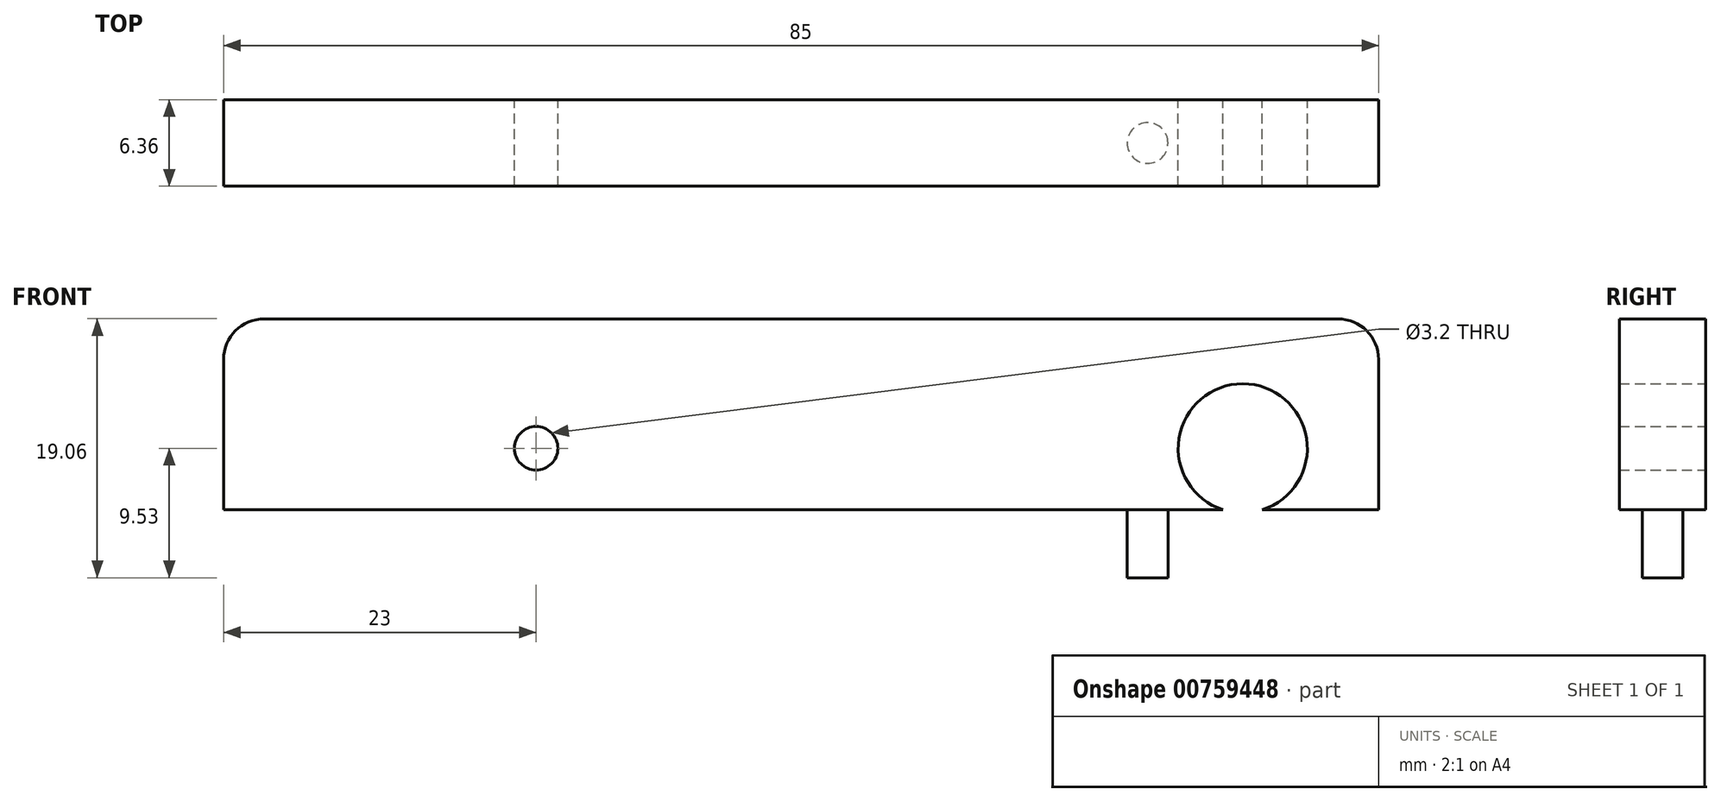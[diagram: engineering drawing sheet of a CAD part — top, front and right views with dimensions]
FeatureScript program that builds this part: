
annotation { "Feature Type Name" : "Feature", "Feature Type Description" : "" }
export const myFeature = defineFeature(function(context is Context, id is Id, definition is map)
    precondition{}
    {
        {
            var Q0;
            Q0=qCreatedBy(makeId("Front.planeOp"),FACE);
            var sketch = newSketch(context, id + "F0", { "sketchPlane" : qUnion([Q0])});
            skLineSegment(sketch, "E0.bottom", {"start": v(42.5, 9.53) * mm, "end": v(-42.5, 9.53) * mm});
            skLineSegment(sketch, "E0.top", {"start": v(42.5, -9.53) * mm, "end": v(-42.5, -9.53) * mm});
            skLineSegment(sketch, "E0.left", {"start": v(42.5, 9.53) * mm, "end": v(42.5, -9.52) * mm});
            skLineSegment(sketch, "E0.right", {"start": v(-42.5, 9.53) * mm, "end": v(-42.5, -9.53) * mm});
            skPoint(sketch, "E0.middle", {"position": v(0, 0) * mm});
            skPoint(sketch, "E1.center.orphan", {"position": v(32.5, 0) * mm});
            skCircle(sketch, "E2", {"center": v(32.5, 0) * mm, "radius": 4.75 * mm});
            skCircle(sketch, "E3", {"center": v(-19.5, 0) * mm, "radius": 1.6 * mm});
            skSolve(sketch);
        }
        {
            var Q0;
            Q0=makeQuery(id+"F0.imprint","IMPRINT",FACE,{"disambiguationData":[TD([[makeQuery(id+"F0.imprint","IMPRINT",EDGE,{"derivedFrom":sQuery(id+"F0.wireOp",EDGE,"E0.bottom")}),1.0]])]});
            extrude(context, id + "F1", {"entities" : qUnion([Q0]), "endBound" : BoundingType.SYMMETRIC, "depth" : 6.35 * mm, "offsetDistance" : 25 * mm});
        }
        {
            var Q0;
            Q0=makeQuery(id+"F1.opExtrude","SWEPT_FACE",FACE,{"disambiguationData":[OSD([sQuery(id+"F0.wireOp",EDGE,"E0.top")])]});
            var sketch = newSketch(context, id + "F2", { "sketchPlane" : qUnion([Q0])});
            skCircle(sketch, "E4", {"center": v(-25.5, 0) * mm, "radius": 1.5 * mm});
            skCircle(sketch, "E5.MirrorC", {"center": v(25.5, 0) * mm, "radius": 1.5 * mm});
            skSolve(sketch);
        }
        {
            var Q0;
            Q0=makeQuery(id+"F2.imprint","IMPRINT",FACE,{"disambiguationData":[TD([[makeQuery(id+"F2.imprint","IMPRINT",EDGE,{"derivedFrom":sQuery(id+"F2.wireOp",EDGE,"E4")}),1.0]])]});
            var Q1;
            Q1=makeQuery(id+"F2.imprint","IMPRINT",FACE,{"disambiguationData":[TD([[makeQuery(id+"F2.imprint","IMPRINT",EDGE,{"derivedFrom":sQuery(id+"F2.wireOp",EDGE,"E5.MirrorC")}),-1.0]])]});
            extrude(context, id + "F3", {"entities" : qUnion([Q0, Q1]), "operationType" : NewBodyOperationType.REMOVE, "oppositeDirection" : true, "depth" : 5 * mm, "offsetDistance" : 25 * mm});
        }
        {
            var Q0;
            Q0=makeQuery(id+"F1.opExtrude","SWEPT_EDGE",EDGE,{"disambiguationData":[OSD([sQuery(id+"F0.wireOp",EDGE,"E0.bottom"),sQuery(id+"F0.wireOp",EDGE,"E0.left")])]});
            fillet(context, id + "F4", {"entities" : qUnion([Q0]), "radius" : 3 * mm, "tangentPropagation" : true, "allowEdgeOverflow" : false});
        }
        {
            var Q0;
            Q0=makeQuery(id+"F1.opExtrude","SWEPT_EDGE",EDGE,{"disambiguationData":[OSD([sQuery(id+"F0.wireOp",EDGE,"E0.bottom"),sQuery(id+"F0.wireOp",EDGE,"E0.right")])]});
            var Q1;
            Q1=makeQuery(id+"F1.opExtrude","SWEPT_EDGE",EDGE,{"disambiguationData":[OSD([sQuery(id+"F0.wireOp",EDGE,"E0.top"),sQuery(id+"F0.wireOp",EDGE,"E0.right")])]});
            var Q2;
            Q2=makeQuery(id+"F1.opExtrude","SWEPT_EDGE",EDGE,{"disambiguationData":[OSD([sQuery(id+"F0.wireOp",EDGE,"E0.top"),sQuery(id+"F0.wireOp",EDGE,"E0.left")])]});
            fillet(context, id + "F5", {"entities" : qUnion([Q0, Q1, Q2]), "radius" : 3 * mm, "tangentPropagation" : true, "allowEdgeOverflow" : false});
        }
    });
